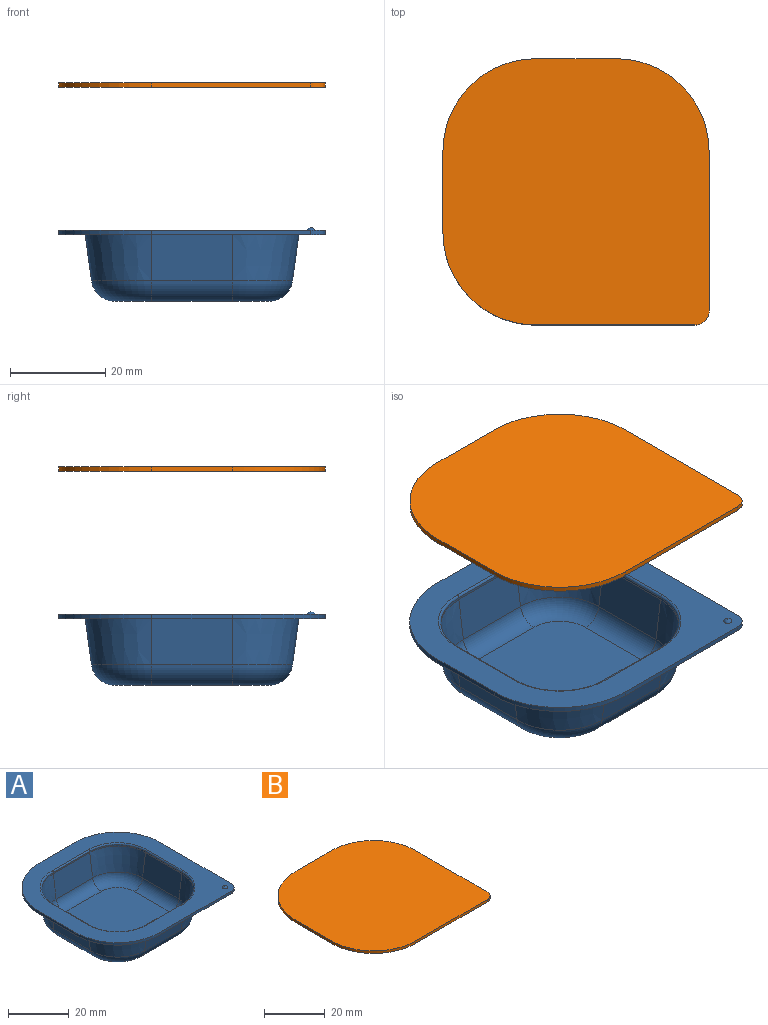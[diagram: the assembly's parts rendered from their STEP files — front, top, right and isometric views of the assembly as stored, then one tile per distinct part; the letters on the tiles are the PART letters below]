
ASSEMBLY  parts=2 mates=1
PART A: 61 faces, bbox 56x56x15.5 mm
  f0: plane 17.02x9.58mm, normal (0,-0.99,0.14), area 164.1mm2, adj f1,f7,f14,f32
  f1: cone r=13.01mm half-angle=8deg, axis (0,0,1), area 186.8mm2, adj f0,f2,f16,f23
  f2: plane 17.02x9.58mm, normal (0.99,0,0.14), area 164.1mm2, adj f1,f3,f15,f22
  f3: cone r=13.01mm half-angle=8deg, axis (0,0,1), area 186.8mm2, adj f2,f4,f13,f21
  f4: plane 17.02x9.58mm, normal (0,0.99,0.14), area 164.1mm2, adj f3,f5,f11,f20
  f5: cone r=13.01mm half-angle=8deg, axis (0,0,1), area 186.8mm2, adj f4,f6,f9,f19
  f6: plane 17.02x9.58mm, normal (-0.99,0,0.14), area 164.1mm2, adj f5,f7,f10,f18
  f7: cone r=13.01mm half-angle=8deg, axis (0,0,1), area 186.8mm2, adj f0,f6,f12,f17
  f8: plane 32.37x32.37mm, normal (0,0,1), area 997.2mm2, adj f9,f10,f11,f12,f13,f14,f15,f16
  f9: torus R=7.69mm, axis (0,0,1), area 90.7mm2, adj f5,f8,f10,f11
  f10: cylinder r=4mm len=17mm, axis (0,1,0), area 97.3mm2, adj f6,f8,f9,f12
  f11: cylinder r=4mm len=17mm, axis (1,0,0), area 97.3mm2, adj f4,f8,f9,f13
  f12: torus R=7.69mm, axis (0,0,1), area 90.7mm2, adj f7,f8,f10,f14
  f13: torus R=7.69mm, axis (0,0,1), area 90.7mm2, adj f3,f8,f11,f15
  f14: cylinder r=4mm len=17mm, axis (1,0,0), area 97.3mm2, adj f0,f8,f12,f16
  f15: cylinder r=4mm len=17mm, axis (0,1,0), area 97.3mm2, adj f2,f8,f13,f16
  f16: torus R=7.69mm, axis (0,0,1), area 90.7mm2, adj f1,f8,f14,f15
  f17: cylinder r=13mm len=13mm, axis (0,0,-1), area 10.2mm2, adj f7,f18,f32,f56
  f18: plane 17.02x0.52mm, normal (-1,0,0), area 8.5mm2, adj f6,f17,f19,f58
  f19: cylinder r=13mm len=13mm, axis (0,0,-1), area 10.2mm2, adj f5,f18,f20,f59
  f20: plane 17.02x0.52mm, normal (0,1,0), area 8.5mm2, adj f4,f19,f21,f57
  f21: cylinder r=13mm len=13mm, axis (0,0,-1), area 10.2mm2, adj f3,f20,f22,f55
  f22: plane 17.02x0.52mm, normal (1,0,0), area 8.5mm2, adj f2,f21,f23,f53
  f23: cylinder r=13mm len=13mm, axis (0,0,-1), area 10.2mm2, adj f1,f22,f32,f52
  f24: plane 17x1mm, normal (0,1,0), area 17mm2, adj f25,f31,f33,f34
  f25: cylinder r=19.5mm len=19.5mm, axis (0,0,-1), area 30.6mm2, adj f24,f26,f33,f34
  f26: plane 17x1mm, normal (-1,0,0), area 17mm2, adj f25,f27,f33,f34
  f27: cylinder r=19.5mm len=19.5mm, axis (0,0,-1), area 30.6mm2, adj f26,f28,f33,f34
  f28: plane 33.5x1mm, normal (0,-1,0), area 33.5mm2, adj f27,f29,f33,f34
  f29: cylinder r=3mm len=3mm, axis (0,0,-1), area 4.7mm2, adj f28,f30,f33,f34
  f30: plane 33.5x1mm, normal (1,0,0), area 33.5mm2, adj f29,f31,f33,f34
  f31: cylinder r=19.5mm len=19.5mm, axis (0,0,-1), area 30.6mm2, adj f24,f30,f33,f34
  f32: plane 17.02x0.52mm, normal (0,-1,0), area 8.5mm2, adj f0,f17,f23,f54
  f33: plane 56x56mm, normal (0,0,1), area 1107.4mm2, adj f24,f25,f26,f27,f28,f29,f30,f31
  f34: plane 56x56mm, normal (0,0,-1), area 1032.5mm2, adj f24,f25,f26,f27,f28,f29,f30,f31
  f35: plane 32.37x32.37mm, normal (0,0,-1), area 997.2mm2, adj f36,f37,f38,f39,f40,f41,f42,f43
  f36: cylinder r=5mm len=17mm, axis (1,0,0), area 121.6mm2, adj f35,f37,f43,f51
  f37: torus R=7.69mm, axis (0,0,1), area 120.2mm2, adj f35,f36,f38,f50
  f38: cylinder r=5mm len=17mm, axis (0,1,0), area 121.6mm2, adj f35,f37,f39,f49
  f39: torus R=7.69mm, axis (0,0,1), area 120.2mm2, adj f35,f38,f40,f48
  f40: cylinder r=5mm len=17mm, axis (1,0,0), area 121.6mm2, adj f35,f39,f41,f47
  f41: torus R=7.69mm, axis (0,0,1), area 120.2mm2, adj f35,f40,f42,f46
  f42: cylinder r=5mm len=17mm, axis (0,1,0), area 121.6mm2, adj f35,f41,f43,f45
  f43: torus R=7.69mm, axis (0,0,1), area 120.2mm2, adj f35,f36,f42,f44
  f44: cone r=14mm half-angle=8deg, axis (0,0,1), area 204.8mm2, adj f34,f43,f45,f51
  f45: plane 17x9.7mm, normal (0.99,0,-0.14), area 166.4mm2, adj f34,f42,f44,f46
  f46: cone r=14mm half-angle=8deg, axis (0,0,1), area 204.8mm2, adj f34,f41,f45,f47
  f47: plane 17x9.7mm, normal (0,-0.99,-0.14), area 166.4mm2, adj f34,f40,f46,f48
  f48: cone r=14mm half-angle=8deg, axis (0,0,1), area 204.8mm2, adj f34,f39,f47,f49
  f49: plane 17x9.7mm, normal (-0.99,0,-0.14), area 166.4mm2, adj f34,f38,f48,f50
  f50: cone r=14mm half-angle=8deg, axis (0,0,1), area 204.8mm2, adj f34,f37,f49,f51
  f51: plane 17x9.7mm, normal (0,0.99,-0.14), area 166.4mm2, adj f34,f36,f44,f50
  f52: torus R=13.5mm, axis (0,0,1), area 16.3mm2, adj f23,f33,f53,f54
  f53: cylinder r=0.5mm len=17mm, axis (0,-1,0), area 13.4mm2, adj f22,f33,f52,f55
  f54: cylinder r=0.5mm len=17mm, axis (-1,0,0), area 13.4mm2, adj f32,f33,f52,f56
  f55: torus R=13.5mm, axis (0,0,1), area 16.3mm2, adj f21,f33,f53,f57
  f56: torus R=13.5mm, axis (0,0,1), area 16.3mm2, adj f17,f33,f54,f58
  f57: cylinder r=0.5mm len=17mm, axis (1,0,0), area 13.4mm2, adj f20,f33,f55,f59
  f58: cylinder r=0.5mm len=17mm, axis (0,1,0), area 13.4mm2, adj f18,f33,f56,f59
  f59: torus R=13.5mm, axis (0,0,1), area 16.3mm2, adj f19,f33,f57,f58
  f60: sphere r=1mm, area 3.1mm2, adj f33
PART B: 10 faces, bbox 56x56x1 mm
  f0: plane 17x1mm, normal (0,1,0), area 17mm2, adj f1,f7,f8,f9
  f1: cylinder r=19.5mm len=19.5mm, axis (0,0,-1), area 30.6mm2, adj f0,f2,f8,f9
  f2: plane 17x1mm, normal (-1,0,0), area 17mm2, adj f1,f3,f8,f9
  f3: cylinder r=19.5mm len=19.5mm, axis (0,0,-1), area 30.6mm2, adj f2,f4,f8,f9
  f4: plane 33.5x1mm, normal (0,-1,0), area 33.5mm2, adj f3,f5,f8,f9
  f5: cylinder r=3mm len=3mm, axis (0,0,-1), area 4.7mm2, adj f4,f6,f8,f9
  f6: plane 33.5x1mm, normal (1,0,0), area 33.5mm2, adj f5,f7,f8,f9
  f7: cylinder r=19.5mm len=19.5mm, axis (0,0,-1), area 30.6mm2, adj f0,f6,f8,f9
  f8: plane 56x56mm, normal (0,0,1), area 2889.3mm2, adj f0,f1,f2,f3,f4,f5,f6,f7
  f9: plane 56x56mm, normal (0,0,-1), area 2889.3mm2, adj f0,f1,f2,f3,f4,f5,f6,f7
PLACE A t=(-3.04,7.57,-17.52)mm
PLACE B t=(-3.04,7.57,13.48)mm
MATE fastened A.f3 <-> B.f3  axis (0,0,1) through (-11.54,-0.93,-16.52)mm
